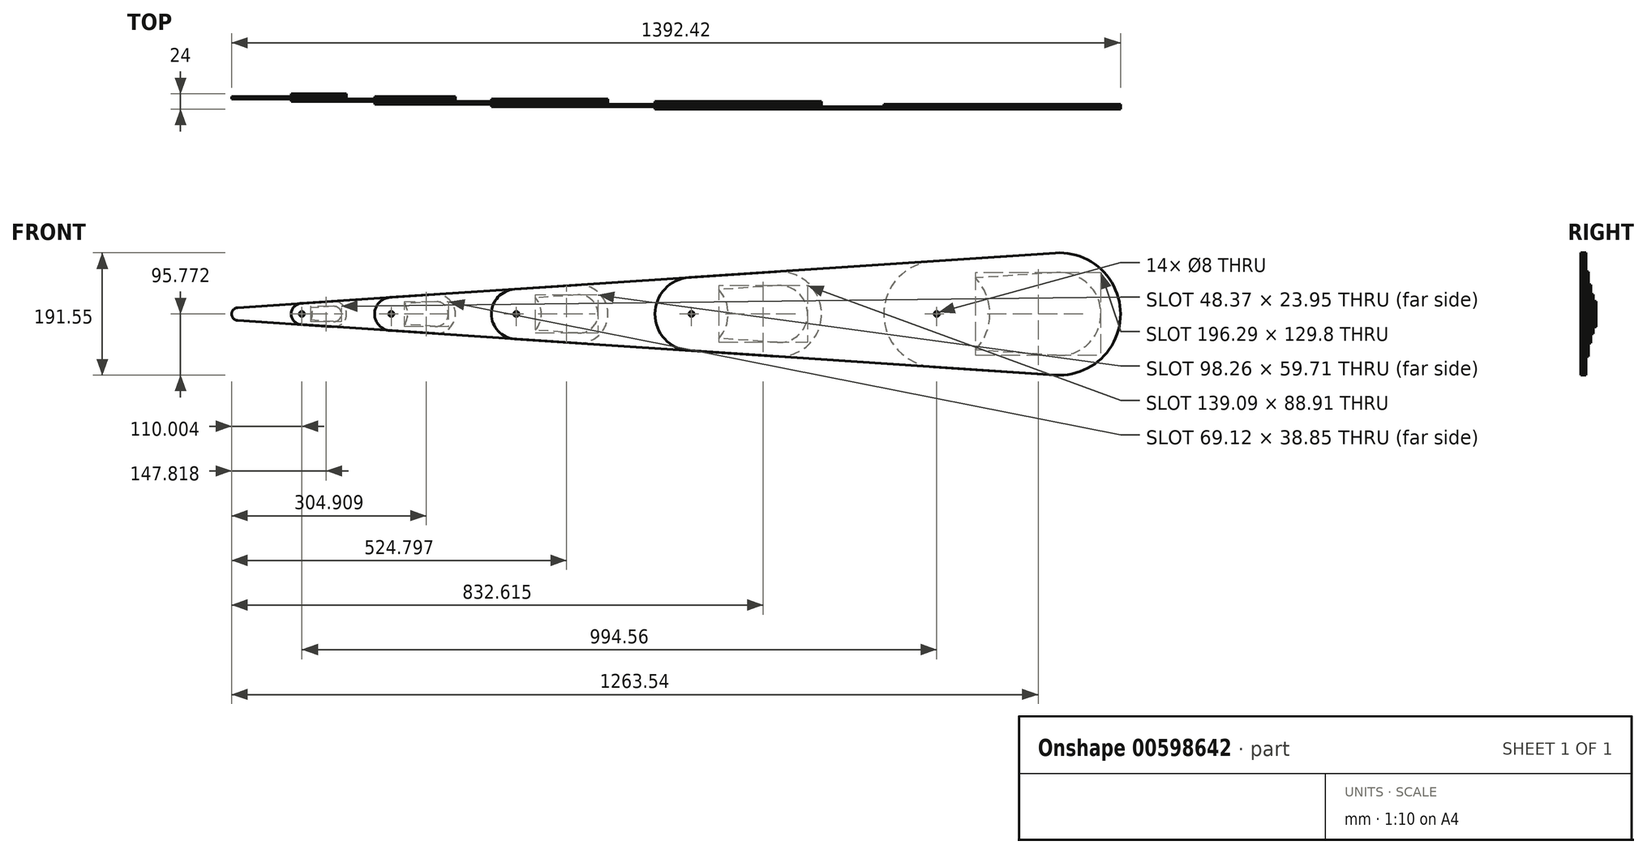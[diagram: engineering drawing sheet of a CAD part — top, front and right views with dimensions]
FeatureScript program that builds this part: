
annotation { "Feature Type Name" : "Feature", "Feature Type Description" : "" }
export const myFeature = defineFeature(function(context is Context, id is Id, definition is map)
    precondition{}
    {
        {
            var Q0;
            Q0=qCreatedBy(makeId("Front.planeOp"),FACE);
            var sketch = newSketch(context, id + "F0", { "sketchPlane" : qUnion([Q0])});
            skCircle(sketch, "E0", {"center": v(13.66, 36.73) * mm, "radius": 20 * mm});
            skCircle(sketch, "E1", {"center": v(-136.34, 36.73) * mm, "radius": 10 * mm});
            skLineSegment(sketch, "E2", {"start": v(12.33, 16.78) * mm, "end": v(-137, 26.75) * mm});
            skLineSegment(sketch, "E3", {"start": v(12.33, 56.69) * mm, "end": v(-137, 46.7) * mm});
            skLineSegment(sketch, "E4", {"start": v(-136.34, 36.73) * mm, "end": v(-36.34, 36.73) * mm, "construction": true});
            skLineSegment(sketch, "E5", {"start": v(-36.34, 36.73) * mm, "end": v(13.66, 36.73) * mm, "construction": true});
            skCircle(sketch, "E6", {"center": v(-36.34, 36.73) * mm, "radius": 4 * mm});
            skSolve(sketch);
        }
        {
            var Q0;
            {var subQ0=sQuery(id+"F0.wireOp",EDGE,"E2");Q0=makeQuery(id+"F0.imprint","IMPRINT",FACE,{"disambiguationData":[TD([[makeQuery(id+"F0.imprint","IMPRINT",EDGE,{"derivedFrom":subQ0}),-1.0]])]});}
            var Q1;
            {var subQ0=sQuery(id+"F0.wireOp",EDGE,"E1");var subQ1=makeQuery(id+"F0.imprint","INTERSECT",VERTEX,{"derivedFrom":[subQ0,sQuery(id+"F0.wireOp",EDGE,"E2")]});Q1=makeQuery(id+"F0.imprint","IMPRINT",FACE,{"disambiguationData":[TD([[makeQuery(id+"F0.imprint","IMPRINT",EDGE,{"disambiguationData":[TD([[subQ1,1.0]])],"derivedFrom":subQ0}),1.0]])]});}
            var Q2;
            {var subQ0=sQuery(id+"F0.wireOp",EDGE,"E0");var subQ1=makeQuery(id+"F0.imprint","INTERSECT",VERTEX,{"derivedFrom":[subQ0,sQuery(id+"F0.wireOp",EDGE,"E2")]});Q2=makeQuery(id+"F0.imprint","IMPRINT",FACE,{"disambiguationData":[TD([[makeQuery(id+"F0.imprint","IMPRINT",EDGE,{"disambiguationData":[TD([[subQ1,1.0]])],"derivedFrom":subQ0}),1.0]])]});}
            extrude(context, id + "F1", {"entities" : qUnion([Q0, Q1, Q2]), "depth" : 4 * mm, "offsetDistance" : 25 * mm});
        }
        {
            var Q0;
            Q0=makeQuery(id+"F1.opExtrude","CAP_FACE",FACE,{"disambiguationData":[OSD([sQuery(id+"F0.wireOp",EDGE,"E0"),sQuery(id+"F0.wireOp",EDGE,"E1"),sQuery(id+"F0.wireOp",EDGE,"E2"),sQuery(id+"F0.wireOp",EDGE,"E3"),sQuery(id+"F0.wireOp",EDGE,"E6")])],"isStart":true});
            var sketch = newSketch(context, id + "F2", { "sketchPlane" : qUnion([Q0])});
            skArc(sketch, "E7", {"start": v(37.45, 20.1) * mm, "mid": v(53, 36.73) * mm, "end": v(37.45, 53.36) * mm});
            skArc(sketch, "E8.0", {"start": v(-12.33, 16.78) * mm, "mid": v(-33.66, 36.73) * mm, "end": v(-12.33, 56.69) * mm});
            skLineSegment(sketch, "E9", {"start": v(-12.33, 56.69) * mm, "end": v(37.45, 53.36) * mm});
            skLineSegment(sketch, "E10", {"start": v(-12.33, 16.78) * mm, "end": v(37.45, 20.1) * mm});
            skCircle(sketch, "E11", {"center": v(36.34, 36.73) * mm, "radius": 16.67 * mm});
            skLineSegment(sketch, "E12.0", {"start": v(-12.86, 48.7) * mm, "end": v(36.91, 45.38) * mm});
            skArc(sketch, "E12.1", {"start": v(-12.86, 24.76) * mm, "mid": v(-25.66, 36.73) * mm, "end": v(-12.86, 48.7) * mm});
            skLineSegment(sketch, "E12.2", {"start": v(-12.86, 24.76) * mm, "end": v(36.91, 28.08) * mm});
            skSolve(sketch);
        }
        {
            var Q0;
            Q0=makeQuery(id+"F2.imprint","IMPRINT",FACE,{"disambiguationData":[TD([[makeQuery(id+"F2.imprint","IMPRINT",EDGE,{"derivedFrom":sQuery(id+"F2.wireOp",EDGE,"E8.0")}),-1.0]])]});
            var Q1;
            Q1=makeQuery(id+"F2.imprint","IMPRINT",FACE,{"disambiguationData":[TD([[makeQuery(id+"F2.imprint","IMPRINT",EDGE,{"derivedFrom":makeQuery(id+"F1.opExtrude","CAP_EDGE",EDGE,{"disambiguationData":[OSD([sQuery(id+"F0.wireOp",EDGE,"E6")])],"isStart":true})}),1.0]])]});
            extrude(context, id + "F3", {"entities" : qUnion([Q0, Q1]), "depth" : 4 * mm, "offsetDistance" : 25 * mm});
        }
        {
            var Q0;
            Q0=makeQuery(id+"F1.opExtrude","CAP_FACE",FACE,{"disambiguationData":[OSD([sQuery(id+"F0.wireOp",EDGE,"E0"),sQuery(id+"F0.wireOp",EDGE,"E1"),sQuery(id+"F0.wireOp",EDGE,"E2"),sQuery(id+"F0.wireOp",EDGE,"E3"),sQuery(id+"F0.wireOp",EDGE,"E6")])],"isStart":false});
            var sketch = newSketch(context, id + "F4", { "sketchPlane" : qUnion([Q0])});
            skCircle(sketch, "E13", {"center": v(-36.34, 36.73) * mm, "radius": 16.67 * mm});
            skLineSegment(sketch, "E14", {"start": v(-36.34, 36.73) * mm, "end": v(103.66, 36.73) * mm, "construction": true});
            skPoint(sketch, "E14.endSnap0", {"position": v(33.66, 36.73) * mm});
            skCircle(sketch, "E15", {"center": v(173.66, 36.73) * mm, "radius": 30.67 * mm});
            skLineSegment(sketch, "E16", {"start": v(171.62, 67.33) * mm, "end": v(-37.45, 53.36) * mm});
            skLineSegment(sketch, "E17", {"start": v(-37.45, 20.1) * mm, "end": v(171.62, 6.13) * mm});
            skLineSegment(sketch, "E18", {"start": v(103.66, 36.73) * mm, "end": v(173.66, 36.73) * mm, "construction": true});
            skCircle(sketch, "E19", {"center": v(103.66, 36.73) * mm, "radius": 4 * mm});
            skSolve(sketch);
        }
        {
            var Q0;
            Q0=makeQuery(id+"F4.imprint","IMPRINT",FACE,{"disambiguationData":[TD([[makeQuery(id+"F4.imprint","IMPRINT",EDGE,{"derivedFrom":makeQuery(id+"F1.opExtrude","CAP_EDGE",EDGE,{"disambiguationData":[OSD([sQuery(id+"F0.wireOp",EDGE,"E6")])],"isStart":false})}),-1.0]])]});
            var Q1;
            Q1=makeQuery(id+"F4.imprint","IMPRINT",FACE,{"disambiguationData":[TD([[makeQuery(id+"F4.imprint","IMPRINT",EDGE,{"derivedFrom":sQuery(id+"F4.wireOp",EDGE,"E19")}),-1.0]])]});
            var Q2;
            {var subQ5=makeQuery(id+"F1.opExtrude","CAP_EDGE",EDGE,{"disambiguationData":[OSD([sQuery(id+"F0.wireOp",EDGE,"E0")])],"isStart":false});Q2=makeQuery(id+"F4.imprint","IMPRINT",FACE,{"disambiguationData":[TD([[makeQuery(id+"F4.imprint","IMPRINT",EDGE,{"derivedFrom":subQ5}),1.0]])]});}
            var Q3;
            {var subQ0=sQuery(id+"F4.wireOp",EDGE,"E15");var subQ1=makeQuery(id+"F4.imprint","INTERSECT",VERTEX,{"derivedFrom":[subQ0,sQuery(id+"F4.wireOp",EDGE,"E16")]});Q3=makeQuery(id+"F4.imprint","IMPRINT",FACE,{"disambiguationData":[TD([[makeQuery(id+"F4.imprint","IMPRINT",EDGE,{"disambiguationData":[TD([[subQ1,-1.0]])],"derivedFrom":subQ0}),1.0]])]});}
            extrude(context, id + "F5", {"entities" : qUnion([Q0, Q1, Q2, Q3]), "depth" : 4 * mm, "offsetDistance" : 25 * mm});
        }
        {
            var Q0;
            Q0=makeQuery(id+"F5.opExtrude","CAP_FACE",FACE,{"disambiguationData":[OSD([sQuery(id+"F0.wireOp",EDGE,"E6"),sQuery(id+"F4.wireOp",EDGE,"E13"),sQuery(id+"F4.wireOp",EDGE,"E15"),sQuery(id+"F4.wireOp",EDGE,"E16"),sQuery(id+"F4.wireOp",EDGE,"E17"),sQuery(id+"F4.wireOp",EDGE,"E19")])],"isStart":true});
            var sketch = newSketch(context, id + "F6", { "sketchPlane" : qUnion([Q0])});
            skCircle(sketch, "E20", {"center": v(-103.66, 36.73) * mm, "radius": 26 * mm});
            skArc(sketch, "E21.0", {"start": v(-171.62, 6.13) * mm, "mid": v(-204.33, 36.73) * mm, "end": v(-171.62, 67.33) * mm});
            skLineSegment(sketch, "E22", {"start": v(-171.62, 67.33) * mm, "end": v(-101.93, 62.67) * mm});
            skLineSegment(sketch, "E23", {"start": v(-171.62, 6.13) * mm, "end": v(-101.93, 10.79) * mm});
            skLineSegment(sketch, "E24.0", {"start": v(-172.37, 56.15) * mm, "end": v(-102.68, 51.5) * mm});
            skArc(sketch, "E24.1", {"start": v(-172.37, 17.3) * mm, "mid": v(-193.13, 36.73) * mm, "end": v(-172.37, 56.15) * mm});
            skLineSegment(sketch, "E24.2", {"start": v(-172.37, 17.3) * mm, "end": v(-102.68, 21.96) * mm});
            skSolve(sketch);
        }
        {
            var Q0;
            Q0=makeQuery(id+"F6.imprint","IMPRINT",FACE,{"disambiguationData":[TD([[makeQuery(id+"F6.imprint","IMPRINT",EDGE,{"derivedFrom":sQuery(id+"F6.wireOp",EDGE,"E21.0")}),-1.0]])]});
            var Q1;
            Q1=makeQuery(id+"F6.imprint","IMPRINT",FACE,{"disambiguationData":[TD([[makeQuery(id+"F6.imprint","IMPRINT",EDGE,{"derivedFrom":makeQuery(id+"F5.opExtrude","CAP_EDGE",EDGE,{"disambiguationData":[OSD([sQuery(id+"F4.wireOp",EDGE,"E19")])],"isStart":true})}),1.0]])]});
            extrude(context, id + "F7", {"entities" : qUnion([Q0, Q1]), "depth" : 4 * mm, "offsetDistance" : 25 * mm});
        }
        {
            var Q0;
            Q0=makeQuery(id+"F5.opExtrude","CAP_FACE",FACE,{"disambiguationData":[OSD([sQuery(id+"F0.wireOp",EDGE,"E6"),sQuery(id+"F4.wireOp",EDGE,"E13"),sQuery(id+"F4.wireOp",EDGE,"E15"),sQuery(id+"F4.wireOp",EDGE,"E16"),sQuery(id+"F4.wireOp",EDGE,"E17"),sQuery(id+"F4.wireOp",EDGE,"E19")])],"isStart":false});
            var sketch = newSketch(context, id + "F8", { "sketchPlane" : qUnion([Q0])});
            skLineSegment(sketch, "E25", {"start": v(103.66, 36.73) * mm, "end": v(299.66, 36.73) * mm, "construction": true});
            skCircle(sketch, "E26", {"center": v(103.66, 36.73) * mm, "radius": 26 * mm});
            skCircle(sketch, "E27", {"center": v(397.66, 36.73) * mm, "radius": 45.6 * mm});
            skLineSegment(sketch, "E28", {"start": v(101.93, 62.67) * mm, "end": v(394.62, 82.23) * mm});
            skLineSegment(sketch, "E29", {"start": v(394.62, -8.77) * mm, "end": v(101.93, 10.79) * mm});
            skLineSegment(sketch, "E30", {"start": v(299.66, 36.73) * mm, "end": v(397.66, 36.73) * mm, "construction": true});
            skCircle(sketch, "E31", {"center": v(299.66, 36.73) * mm, "radius": 4 * mm});
            skSolve(sketch);
        }
        {
            var Q0;
            Q0=makeQuery(id+"F8.imprint","IMPRINT",FACE,{"disambiguationData":[TD([[makeQuery(id+"F8.imprint","IMPRINT",EDGE,{"derivedFrom":makeQuery(id+"F5.opExtrude","CAP_EDGE",EDGE,{"disambiguationData":[OSD([sQuery(id+"F4.wireOp",EDGE,"E19")])],"isStart":false})}),-1.0]])]});
            var Q1;
            {var subQ5=makeQuery(id+"F5.opExtrude","CAP_EDGE",EDGE,{"disambiguationData":[OSD([sQuery(id+"F4.wireOp",EDGE,"E15")])],"isStart":false});Q1=makeQuery(id+"F8.imprint","IMPRINT",FACE,{"disambiguationData":[TD([[makeQuery(id+"F8.imprint","IMPRINT",EDGE,{"derivedFrom":subQ5}),1.0]])]});}
            var Q2;
            Q2=makeQuery(id+"F8.imprint","IMPRINT",FACE,{"disambiguationData":[TD([[makeQuery(id+"F8.imprint","IMPRINT",EDGE,{"derivedFrom":sQuery(id+"F8.wireOp",EDGE,"E31")}),-1.0]])]});
            var Q3;
            {var subQ0=sQuery(id+"F8.wireOp",EDGE,"E27");var subQ1=makeQuery(id+"F8.imprint","INTERSECT",VERTEX,{"derivedFrom":[subQ0,sQuery(id+"F8.wireOp",EDGE,"E28")]});Q3=makeQuery(id+"F8.imprint","IMPRINT",FACE,{"disambiguationData":[TD([[makeQuery(id+"F8.imprint","IMPRINT",EDGE,{"disambiguationData":[TD([[subQ1,-1.0]])],"derivedFrom":subQ0}),1.0]])]});}
            extrude(context, id + "F9", {"entities" : qUnion([Q0, Q1, Q2, Q3]), "depth" : 4 * mm, "offsetDistance" : 25 * mm});
        }
        {
            var Q0;
            Q0=makeQuery(id+"F9.opExtrude","CAP_FACE",FACE,{"disambiguationData":[OSD([sQuery(id+"F4.wireOp",EDGE,"E19"),sQuery(id+"F8.wireOp",EDGE,"E26"),sQuery(id+"F8.wireOp",EDGE,"E27"),sQuery(id+"F8.wireOp",EDGE,"E28"),sQuery(id+"F8.wireOp",EDGE,"E29"),sQuery(id+"F8.wireOp",EDGE,"E31")])],"isStart":true});
            var sketch = newSketch(context, id + "F10", { "sketchPlane" : qUnion([Q0])});
            skCircle(sketch, "E32", {"center": v(-299.66, 36.73) * mm, "radius": 39.07 * mm});
            skArc(sketch, "E33.0", {"start": v(-394.62, -8.77) * mm, "mid": v(-443.26, 36.73) * mm, "end": v(-394.62, 82.23) * mm});
            skLineSegment(sketch, "E34", {"start": v(-394.62, 82.23) * mm, "end": v(-297.06, 75.71) * mm});
            skLineSegment(sketch, "E35", {"start": v(-394.62, -8.77) * mm, "end": v(-297.06, -2.25) * mm});
            skLineSegment(sketch, "E36.0", {"start": v(-395.67, 66.58) * mm, "end": v(-298.1, 60.07) * mm});
            skArc(sketch, "E36.1", {"start": v(-395.67, 6.88) * mm, "mid": v(-427.58, 36.73) * mm, "end": v(-395.67, 66.58) * mm});
            skLineSegment(sketch, "E36.2", {"start": v(-395.67, 6.88) * mm, "end": v(-298.1, 13.4) * mm});
            skSolve(sketch);
        }
        {
            var Q0;
            Q0=makeQuery(id+"F10.imprint","IMPRINT",FACE,{"disambiguationData":[TD([[makeQuery(id+"F10.imprint","IMPRINT",EDGE,{"derivedFrom":sQuery(id+"F10.wireOp",EDGE,"E33.0")}),-1.0]])]});
            var Q1;
            Q1=makeQuery(id+"F10.imprint","IMPRINT",FACE,{"disambiguationData":[TD([[makeQuery(id+"F10.imprint","IMPRINT",EDGE,{"derivedFrom":makeQuery(id+"F9.opExtrude","CAP_EDGE",EDGE,{"disambiguationData":[OSD([sQuery(id+"F8.wireOp",EDGE,"E31")])],"isStart":true})}),1.0]])]});
            extrude(context, id + "F11", {"entities" : qUnion([Q0, Q1]), "depth" : 4 * mm, "offsetDistance" : 25 * mm});
        }
        {
            var Q0;
            Q0=makeQuery(id+"F9.opExtrude","CAP_FACE",FACE,{"disambiguationData":[OSD([sQuery(id+"F4.wireOp",EDGE,"E19"),sQuery(id+"F8.wireOp",EDGE,"E26"),sQuery(id+"F8.wireOp",EDGE,"E27"),sQuery(id+"F8.wireOp",EDGE,"E28"),sQuery(id+"F8.wireOp",EDGE,"E29"),sQuery(id+"F8.wireOp",EDGE,"E31")])],"isStart":false});
            var sketch = newSketch(context, id + "F12", { "sketchPlane" : qUnion([Q0])});
            skCircle(sketch, "E37", {"center": v(299.66, 36.73) * mm, "radius": 39.07 * mm});
            skLineSegment(sketch, "E38", {"start": v(299.66, 36.73) * mm, "end": v(574.06, 36.73) * mm, "construction": true});
            skCircle(sketch, "E39", {"center": v(711.26, 36.73) * mm, "radius": 66.5 * mm});
            skLineSegment(sketch, "E40", {"start": v(297.06, 75.71) * mm, "end": v(706.83, 103.1) * mm});
            skLineSegment(sketch, "E41", {"start": v(297.06, -2.25) * mm, "end": v(706.83, -29.63) * mm});
            skLineSegment(sketch, "E42", {"start": v(574.06, 36.73) * mm, "end": v(711.26, 36.73) * mm, "construction": true});
            skCircle(sketch, "E43", {"center": v(574.06, 36.73) * mm, "radius": 4 * mm});
            skSolve(sketch);
        }
        {
            var Q0;
            Q0=makeQuery(id+"F12.imprint","IMPRINT",FACE,{"disambiguationData":[TD([[makeQuery(id+"F12.imprint","IMPRINT",EDGE,{"derivedFrom":makeQuery(id+"F9.opExtrude","CAP_EDGE",EDGE,{"disambiguationData":[OSD([sQuery(id+"F8.wireOp",EDGE,"E31")])],"isStart":false})}),-1.0]])]});
            var Q1;
            {var subQ5=makeQuery(id+"F9.opExtrude","CAP_EDGE",EDGE,{"disambiguationData":[OSD([sQuery(id+"F8.wireOp",EDGE,"E27")])],"isStart":false});Q1=makeQuery(id+"F12.imprint","IMPRINT",FACE,{"disambiguationData":[TD([[makeQuery(id+"F12.imprint","IMPRINT",EDGE,{"derivedFrom":subQ5}),1.0]])]});}
            var Q2;
            Q2=makeQuery(id+"F12.imprint","IMPRINT",FACE,{"disambiguationData":[TD([[makeQuery(id+"F12.imprint","IMPRINT",EDGE,{"derivedFrom":sQuery(id+"F12.wireOp",EDGE,"E43")}),-1.0]])]});
            var Q3;
            {var subQ0=sQuery(id+"F12.wireOp",EDGE,"E39");var subQ1=makeQuery(id+"F12.imprint","INTERSECT",VERTEX,{"derivedFrom":[subQ0,sQuery(id+"F12.wireOp",EDGE,"E40")]});Q3=makeQuery(id+"F12.imprint","IMPRINT",FACE,{"disambiguationData":[TD([[makeQuery(id+"F12.imprint","IMPRINT",EDGE,{"disambiguationData":[TD([[subQ1,-1.0]])],"derivedFrom":subQ0}),1.0]])]});}
            extrude(context, id + "F13", {"entities" : qUnion([Q0, Q1, Q2, Q3]), "depth" : 4 * mm, "offsetDistance" : 25 * mm});
        }
        {
            var Q0;
            Q0=makeQuery(id+"F13.opExtrude","CAP_FACE",FACE,{"disambiguationData":[OSD([sQuery(id+"F8.wireOp",EDGE,"E31"),sQuery(id+"F12.wireOp",EDGE,"E37"),sQuery(id+"F12.wireOp",EDGE,"E39"),sQuery(id+"F12.wireOp",EDGE,"E40"),sQuery(id+"F12.wireOp",EDGE,"E41"),sQuery(id+"F12.wireOp",EDGE,"E43")])],"isStart":true});
            var sketch = newSketch(context, id + "F14", { "sketchPlane" : qUnion([Q0])});
            skCircle(sketch, "E44", {"center": v(-574.06, 36.73) * mm, "radius": 57.36 * mm});
            skArc(sketch, "E45.0", {"start": v(-706.83, -29.63) * mm, "mid": v(-777.77, 36.73) * mm, "end": v(-706.83, 103.1) * mm});
            skLineSegment(sketch, "E46", {"start": v(-706.83, 103.1) * mm, "end": v(-570.24, 93.96) * mm});
            skLineSegment(sketch, "E47", {"start": v(-706.83, -29.63) * mm, "end": v(-570.24, -20.5) * mm});
            skLineSegment(sketch, "E48.0", {"start": v(-708.3, -7.72) * mm, "end": v(-571.7, 1.4) * mm});
            skArc(sketch, "E48.1", {"start": v(-708.3, -7.72) * mm, "mid": v(-755.82, 36.73) * mm, "end": v(-708.3, 81.19) * mm});
            skLineSegment(sketch, "E48.2", {"start": v(-708.3, 81.19) * mm, "end": v(-571.7, 72.06) * mm});
            skSolve(sketch);
        }
        {
            var Q0;
            Q0=makeQuery(id+"F14.imprint","IMPRINT",FACE,{"disambiguationData":[TD([[makeQuery(id+"F14.imprint","IMPRINT",EDGE,{"derivedFrom":sQuery(id+"F14.wireOp",EDGE,"E45.0")}),-1.0]])]});
            var Q1;
            Q1=makeQuery(id+"F14.imprint","IMPRINT",FACE,{"disambiguationData":[TD([[makeQuery(id+"F14.imprint","IMPRINT",EDGE,{"derivedFrom":makeQuery(id+"F13.opExtrude","CAP_EDGE",EDGE,{"disambiguationData":[OSD([sQuery(id+"F12.wireOp",EDGE,"E43")])],"isStart":true})}),1.0]])]});
            extrude(context, id + "F15", {"entities" : qUnion([Q0, Q1]), "depth" : 4 * mm, "offsetDistance" : 25 * mm});
        }
        {
            var Q0;
            Q0=makeQuery(id+"F13.opExtrude","CAP_FACE",FACE,{"disambiguationData":[OSD([sQuery(id+"F8.wireOp",EDGE,"E31"),sQuery(id+"F12.wireOp",EDGE,"E37"),sQuery(id+"F12.wireOp",EDGE,"E39"),sQuery(id+"F12.wireOp",EDGE,"E40"),sQuery(id+"F12.wireOp",EDGE,"E41"),sQuery(id+"F12.wireOp",EDGE,"E43")])],"isStart":false});
            var sketch = newSketch(context, id + "F16", { "sketchPlane" : qUnion([Q0])});
            skCircle(sketch, "E49", {"center": v(574.06, 36.73) * mm, "radius": 57.36 * mm});
            skLineSegment(sketch, "E50", {"start": v(574.06, 36.73) * mm, "end": v(958.22, 36.73) * mm, "construction": true});
            skPoint(sketch, "E50.endSnap0", {"position": v(777.77, 36.73) * mm});
            skCircle(sketch, "E51", {"center": v(1150.3, 36.73) * mm, "radius": 95.78 * mm});
            skLineSegment(sketch, "E52", {"start": v(570.24, 93.96) * mm, "end": v(1143.92, 132.3) * mm});
            skLineSegment(sketch, "E53", {"start": v(570.24, -20.5) * mm, "end": v(1143.92, -58.83) * mm});
            skLineSegment(sketch, "E54", {"start": v(958.22, 36.73) * mm, "end": v(1150.3, 36.73) * mm, "construction": true});
            skCircle(sketch, "E55", {"center": v(958.22, 36.73) * mm, "radius": 4 * mm});
            skSolve(sketch);
        }
        {
            var Q0;
            Q0=makeQuery(id+"F16.imprint","IMPRINT",FACE,{"disambiguationData":[TD([[makeQuery(id+"F16.imprint","IMPRINT",EDGE,{"derivedFrom":makeQuery(id+"F13.opExtrude","CAP_EDGE",EDGE,{"disambiguationData":[OSD([sQuery(id+"F12.wireOp",EDGE,"E43")])],"isStart":false})}),-1.0]])]});
            var Q1;
            {var subQ5=makeQuery(id+"F13.opExtrude","CAP_EDGE",EDGE,{"disambiguationData":[OSD([sQuery(id+"F12.wireOp",EDGE,"E39")])],"isStart":false});Q1=makeQuery(id+"F16.imprint","IMPRINT",FACE,{"disambiguationData":[TD([[makeQuery(id+"F16.imprint","IMPRINT",EDGE,{"derivedFrom":subQ5}),1.0]])]});}
            var Q2;
            Q2=makeQuery(id+"F16.imprint","IMPRINT",FACE,{"disambiguationData":[TD([[makeQuery(id+"F16.imprint","IMPRINT",EDGE,{"derivedFrom":sQuery(id+"F16.wireOp",EDGE,"E55")}),-1.0]])]});
            var Q3;
            {var subQ0=sQuery(id+"F16.wireOp",EDGE,"E51");var subQ1=makeQuery(id+"F16.imprint","INTERSECT",VERTEX,{"derivedFrom":[subQ0,sQuery(id+"F16.wireOp",EDGE,"E52")]});Q3=makeQuery(id+"F16.imprint","IMPRINT",FACE,{"disambiguationData":[TD([[makeQuery(id+"F16.imprint","IMPRINT",EDGE,{"disambiguationData":[TD([[subQ1,-1.0]])],"derivedFrom":subQ0}),1.0]])]});}
            extrude(context, id + "F17", {"entities" : qUnion([Q0, Q1, Q2, Q3]), "depth" : 4 * mm, "offsetDistance" : 25 * mm});
        }
        {
            var Q0;
            Q0=makeQuery(id+"F17.opExtrude","CAP_FACE",FACE,{"disambiguationData":[OSD([sQuery(id+"F12.wireOp",EDGE,"E43"),sQuery(id+"F16.wireOp",EDGE,"E49"),sQuery(id+"F16.wireOp",EDGE,"E51"),sQuery(id+"F16.wireOp",EDGE,"E52"),sQuery(id+"F16.wireOp",EDGE,"E53"),sQuery(id+"F16.wireOp",EDGE,"E55")])],"isStart":true});
            var sketch = newSketch(context, id + "F18", { "sketchPlane" : qUnion([Q0])});
            skCircle(sketch, "E56", {"center": v(-958.22, 36.73) * mm, "radius": 82.97 * mm});
            skArc(sketch, "E57.0", {"start": v(-1143.92, -58.83) * mm, "mid": v(-1246.08, 36.73) * mm, "end": v(-1143.92, 132.3) * mm});
            skLineSegment(sketch, "E58", {"start": v(-1143.92, 132.3) * mm, "end": v(-952.7, 119.52) * mm});
            skLineSegment(sketch, "E59", {"start": v(-1143.92, -58.83) * mm, "end": v(-952.7, -46.05) * mm});
            skLineSegment(sketch, "E60.0", {"start": v(-1145.97, 101.63) * mm, "end": v(-954.74, 88.85) * mm});
            skArc(sketch, "E60.1", {"start": v(-1145.97, -28.17) * mm, "mid": v(-1215.35, 36.73) * mm, "end": v(-1145.97, 101.63) * mm});
            skLineSegment(sketch, "E60.2", {"start": v(-1145.97, -28.17) * mm, "end": v(-954.74, -15.4) * mm});
            skSolve(sketch);
        }
        {
            var Q0;
            Q0=makeQuery(id+"F18.imprint","IMPRINT",FACE,{"disambiguationData":[TD([[makeQuery(id+"F18.imprint","IMPRINT",EDGE,{"derivedFrom":sQuery(id+"F18.wireOp",EDGE,"E57.0")}),-1.0]])]});
            var Q1;
            Q1=makeQuery(id+"F18.imprint","IMPRINT",FACE,{"disambiguationData":[TD([[makeQuery(id+"F18.imprint","IMPRINT",EDGE,{"derivedFrom":makeQuery(id+"F17.opExtrude","CAP_EDGE",EDGE,{"disambiguationData":[OSD([sQuery(id+"F16.wireOp",EDGE,"E55")])],"isStart":true})}),1.0]])]});
            extrude(context, id + "F19", {"entities" : qUnion([Q0, Q1]), "depth" : 4 * mm, "offsetDistance" : 25 * mm});
        }
    });
